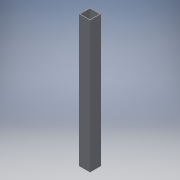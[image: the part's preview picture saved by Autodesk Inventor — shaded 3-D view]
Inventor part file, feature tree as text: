
AUTODESK INVENTOR PART (.ipt)
format: ipt  version: 2016 (Build 200138000, 138)  size: 104,448 bytes
history: native  units: in
note: dims shown in document units (in); Inventor stores cm internally (conversion verified against a paired STEP export)
features: extrude x2, sketch x2
ambient origin geometry x8: Origin, YZ Plane, XZ Plane, XY Plane, X Axis, Y Axis, Z Axis, Center Point
bodies: Solid1 (feature_tree)
feature tree (4):
  extrude  "Extrusion1"  Depth=1.0in
  extrude  "Extrusion2"  Depth=1.0in TaperAngle=0.0deg
  sketch  "Sketch1"  dims[d0=1.0in d1=1.0in]
  sketch  "Sketch2"  dims[d2=0.0625in d3=9.3708in d4=0.0in d5=0.3018in d6=1.0in d7=0.0in]
